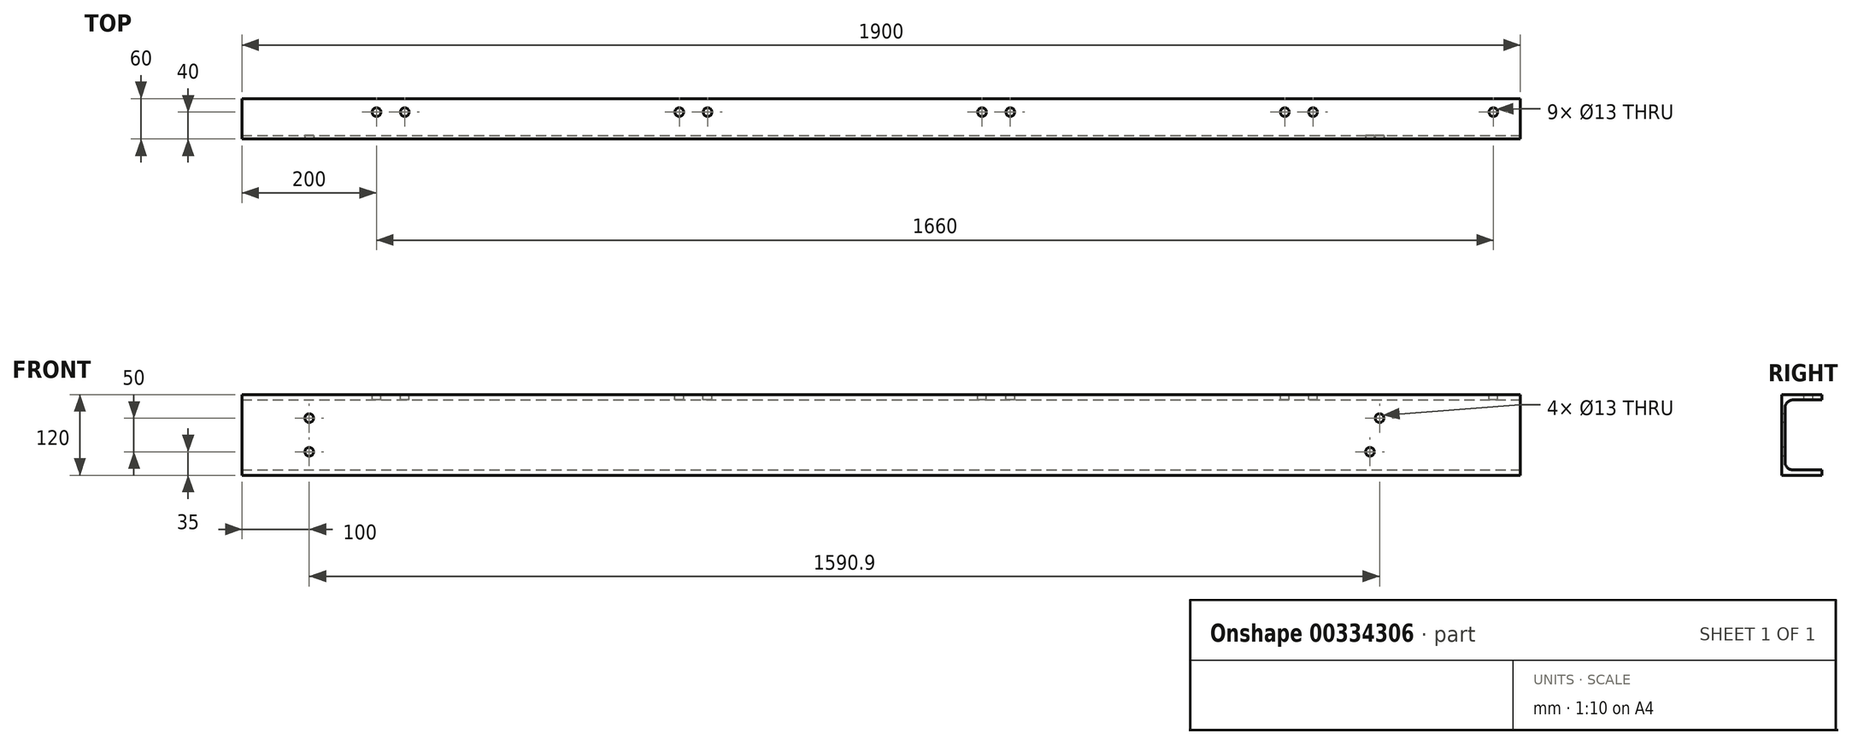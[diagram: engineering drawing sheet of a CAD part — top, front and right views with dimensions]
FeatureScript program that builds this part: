
annotation { "Feature Type Name" : "Feature", "Feature Type Description" : "" }
export const myFeature = defineFeature(function(context is Context, id is Id, definition is map)
    precondition{}
    {
        {
            assignVariable(context, id + "F0", {"name" : "L_Pro", "anyValue" : 1900});
        }
        {
            var Q0;
            Q0=qCreatedBy(makeId("Right.planeOp"),FACE);
            var sketch = newSketch(context, id + "F1", { "sketchPlane" : qUnion([Q0])});
            skLineSegment(sketch, "E0", {"start": v(0, 0) * mm, "end": v(-60, 0) * mm});
            skLineSegment(sketch, "E1", {"start": v(-60, 0) * mm, "end": v(-60, 120) * mm});
            skLineSegment(sketch, "E2", {"start": v(-60, 120) * mm, "end": v(0, 120) * mm});
            skLineSegment(sketch, "E3", {"start": v(0, 120) * mm, "end": v(0, 112) * mm});
            skLineSegment(sketch, "E4", {"start": v(0, 112) * mm, "end": v(-43, 112) * mm});
            skLineSegment(sketch, "E5", {"start": v(-55, 100) * mm, "end": v(-55, 20) * mm});
            skLineSegment(sketch, "E6", {"start": v(-43, 8) * mm, "end": v(0, 8) * mm});
            skLineSegment(sketch, "E7", {"start": v(0, 8) * mm, "end": v(0, 0) * mm});
            skPoint(sketch, "E8.visualSharp", {"position": v(-55, 112) * mm});
            skArc(sketch, "E8.filletArc", {"start": v(-43, 112) * mm, "mid": v(-51.49, 108.49) * mm, "end": v(-55, 100) * mm});
            skPoint(sketch, "E9.visualSharp", {"position": v(-55, 8) * mm});
            skArc(sketch, "E9.filletArc", {"start": v(-55, 20) * mm, "mid": v(-51.49, 11.51) * mm, "end": v(-43, 8) * mm});
            skSolve(sketch);
        }
        {
            var Q0;
            Q0=qSketchRegion(id+"F1",true);
            var Q1;
            Q1=qConstructionFilter(qBodyType(qCreatedBy(id+"F1",EDGE),BodyType.WIRE),ConstructionObject.NO);
            extrude(context, id + "F2", {"entities" : qUnion([Q0]), "surfaceEntities" : qUnion([Q1]), "oppositeDirection" : true, "depth" : (getVariable(context, 'L_Pro')) * mm});
        }
        {
            var Q0;
            Q0=makeQuery(id+"F2.opExtrude","SWEPT_FACE",FACE,{"disambiguationData":[OSD([sQuery(id+"F1.wireOp",EDGE,"E2")])]});
            var sketch = newSketch(context, id + "F3", { "sketchPlane" : qUnion([Q0])});
            skCircle(sketch, "E10", {"center": v(-40, -20) * mm, "radius": 6.5 * mm});
            skCircle(sketch, "E11", {"center": v(-82, -20) * mm, "radius": 6.5 * mm, "construction": true});
            skCircle(sketch, "E12", {"center": v(-758, -20) * mm, "radius": 6.5 * mm});
            skCircle(sketch, "E13", {"center": v(-800, -20) * mm, "radius": 6.5 * mm});
            skCircle(sketch, "E14", {"center": v(-1658, -20) * mm, "radius": 6.5 * mm});
            skCircle(sketch, "E15", {"center": v(-1700, -20) * mm, "radius": 6.5 * mm});
            skCircle(sketch, "E16", {"center": v(-1208, -20) * mm, "radius": 6.5 * mm});
            skCircle(sketch, "E17", {"center": v(-1250, -20) * mm, "radius": 6.5 * mm});
            skCircle(sketch, "E18", {"center": v(-350, -20) * mm, "radius": 6.5 * mm});
            skCircle(sketch, "E19", {"center": v(-308, -20) * mm, "radius": 6.5 * mm});
            skSolve(sketch);
        }
        {
            var Q0;
            Q0=makeQuery(id+"F3.imprint","IMPRINT",FACE,{"disambiguationData":[TD([[makeQuery(id+"F3.imprint","IMPRINT",EDGE,{"derivedFrom":sQuery(id+"F3.wireOp",EDGE,"E11")}),1.0]])]});
            var Q1;
            Q1=makeQuery(id+"F3.imprint","IMPRINT",FACE,{"disambiguationData":[TD([[makeQuery(id+"F3.imprint","IMPRINT",EDGE,{"derivedFrom":sQuery(id+"F3.wireOp",EDGE,"E10")}),1.0]])]});
            var Q2;
            Q2=makeQuery(id+"F3.imprint","IMPRINT",FACE,{"disambiguationData":[TD([[makeQuery(id+"F3.imprint","IMPRINT",EDGE,{"derivedFrom":sQuery(id+"F3.wireOp",EDGE,"E12")}),1.0]])]});
            var Q3;
            Q3=makeQuery(id+"F3.imprint","IMPRINT",FACE,{"disambiguationData":[TD([[makeQuery(id+"F3.imprint","IMPRINT",EDGE,{"derivedFrom":sQuery(id+"F3.wireOp",EDGE,"E13")}),1.0]])]});
            var Q4;
            Q4=makeQuery(id+"F3.imprint","IMPRINT",FACE,{"disambiguationData":[TD([[makeQuery(id+"F3.imprint","IMPRINT",EDGE,{"derivedFrom":sQuery(id+"F3.wireOp",EDGE,"E14")}),1.0]])]});
            var Q5;
            Q5=makeQuery(id+"F3.imprint","IMPRINT",FACE,{"disambiguationData":[TD([[makeQuery(id+"F3.imprint","IMPRINT",EDGE,{"derivedFrom":sQuery(id+"F3.wireOp",EDGE,"E15")}),1.0]])]});
            var Q6;
            Q6=makeQuery(id+"F3.imprint","IMPRINT",FACE,{"disambiguationData":[TD([[makeQuery(id+"F3.imprint","IMPRINT",EDGE,{"derivedFrom":sQuery(id+"F3.wireOp",EDGE,"Qfvc6uuf-Tqhu-fWyK-ezUu-9xUIy1GmAbfD")}),1.0]])]});
            var Q7;
            Q7=makeQuery(id+"F3.imprint","IMPRINT",FACE,{"disambiguationData":[TD([[makeQuery(id+"F3.imprint","IMPRINT",EDGE,{"derivedFrom":sQuery(id+"F3.wireOp",EDGE,"OamrkCoK-SCLr-TKa5-v8dG-G0AeQ86CE51D")}),1.0]])]});
            var Q8;
            Q8=makeQuery(id+"F3.imprint","IMPRINT",FACE,{"disambiguationData":[TD([[makeQuery(id+"F3.imprint","IMPRINT",EDGE,{"derivedFrom":sQuery(id+"F3.wireOp",EDGE,"E16")}),1.0]])]});
            var Q9;
            Q9=makeQuery(id+"F3.imprint","IMPRINT",FACE,{"disambiguationData":[TD([[makeQuery(id+"F3.imprint","IMPRINT",EDGE,{"derivedFrom":sQuery(id+"F3.wireOp",EDGE,"E17")}),1.0]])]});
            var Q10;
            Q10=makeQuery(id+"F3.imprint","IMPRINT",FACE,{"disambiguationData":[TD([[makeQuery(id+"F3.imprint","IMPRINT",EDGE,{"derivedFrom":sQuery(id+"F3.wireOp",EDGE,"E18")}),1.0]])]});
            var Q11;
            Q11=makeQuery(id+"F3.imprint","IMPRINT",FACE,{"disambiguationData":[TD([[makeQuery(id+"F3.imprint","IMPRINT",EDGE,{"derivedFrom":sQuery(id+"F3.wireOp",EDGE,"E19")}),1.0]])]});
            extrude(context, id + "F4", {"entities" : qUnion([Q0, Q1, Q2, Q3, Q4, Q5, Q6, Q7, Q8, Q9, Q10, Q11]), "operationType" : NewBodyOperationType.REMOVE, "endBound" : BoundingType.UP_TO_NEXT, "oppositeDirection" : true, "depth" : 25 * mm});
        }
        {
            var Q0;
            Q0=makeQuery(id+"F2.opExtrude","SWEPT_FACE",FACE,{"disambiguationData":[OSD([sQuery(id+"F1.wireOp",EDGE,"E1")])]});
            var sketch = newSketch(context, id + "F5", { "sketchPlane" : qUnion([Q0])});
            skLineSegment(sketch, "E20", {"start": v(-1900, 60) * mm, "end": v(-1758.04, 60) * mm, "construction": true});
            skCircle(sketch, "E21", {"center": v(-1800, 85) * mm, "radius": 6.5 * mm});
            skCircle(sketch, "E22", {"center": v(-1800, 35) * mm, "radius": 6.5 * mm});
            skCircle(sketch, "E23", {"center": v(-223.44, 35) * mm, "radius": 6.5 * mm});
            skLineSegment(sketch, "E24", {"start": v(-223.44, 35) * mm, "end": v(-223.44, 85) * mm, "construction": true});
            skLineSegment(sketch, "E25", {"start": v(-223.44, 35) * mm, "end": v(-209.1, 85) * mm, "construction": true});
            skCircle(sketch, "E26", {"center": v(-209.1, 85) * mm, "radius": 6.5 * mm});
            skSolve(sketch);
        }
        {
            var Q0;
            Q0=qSketchRegion(id+"F5",true);
            extrude(context, id + "F6", {"entities" : qUnion([Q0]), "operationType" : NewBodyOperationType.REMOVE, "endBound" : BoundingType.THROUGH_ALL, "oppositeDirection" : true, "depth" : 25 * mm});
        }
    });
